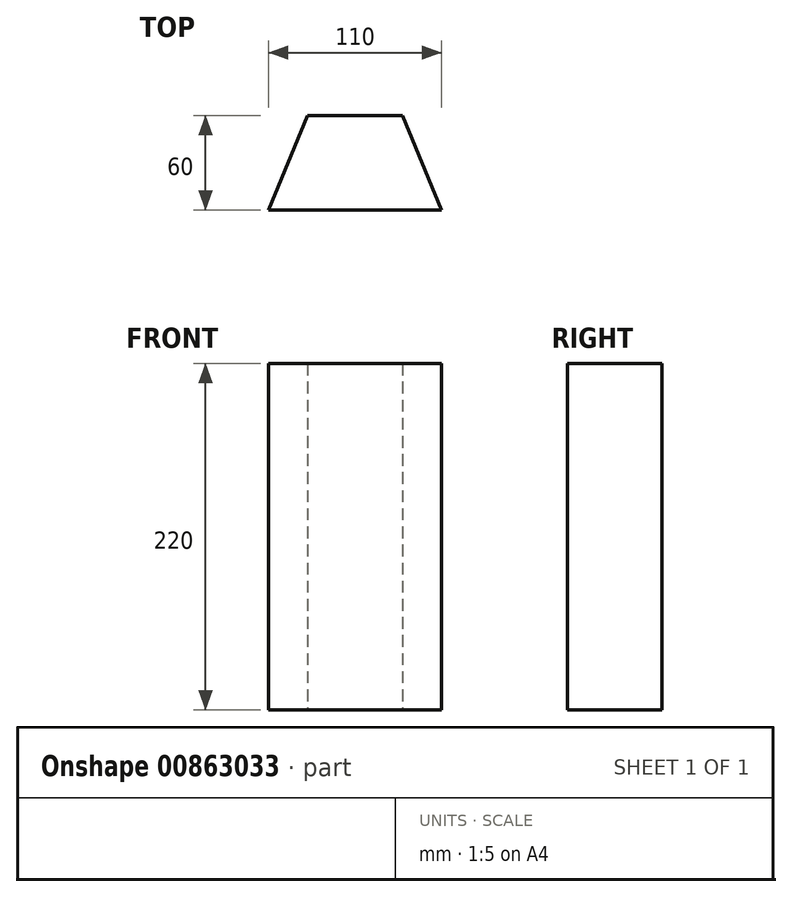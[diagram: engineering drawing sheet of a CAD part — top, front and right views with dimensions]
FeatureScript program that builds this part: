
annotation { "Feature Type Name" : "Feature", "Feature Type Description" : "" }
export const myFeature = defineFeature(function(context is Context, id is Id, definition is map)
    precondition{}
    {
        {
            var Q0;
            Q0=qCreatedBy(makeId("Top.planeOp"),FACE);
            var sketch = newSketch(context, id + "F0", { "sketchPlane" : qUnion([Q0])});
            skLineSegment(sketch, "E0.bottom", {"start": v(55, -60) * mm, "end": v(0, -60) * mm});
            skLineSegment(sketch, "E0.top", {"start": v(30.15, 0) * mm, "end": v(0, 0) * mm});
            skPoint(sketch, "E0.middle", {"position": v(0, 0) * mm});
            skLineSegment(sketch, "E1", {"start": v(55, -60) * mm, "end": v(30.15, 0) * mm});
            skLineSegment(sketch, "E2", {"start": v(0, -60) * mm, "end": v(0, 0) * mm, "construction": true});
            skLineSegment(sketch, "E3.MirrorCS", {"start": v(-55, -60) * mm, "end": v(0, -60) * mm});
            skLineSegment(sketch, "E4.MirrorCS", {"start": v(-55, -60) * mm, "end": v(-30.15, 0) * mm});
            skLineSegment(sketch, "E5.MirrorCS", {"start": v(-30.15, 0) * mm, "end": v(0, 0) * mm});
            skSolve(sketch);
        }
        {
            var Q0;
            Q0 = qSketchRegion(id + "F0", true);
            extrude(context, id + "F1", {"entities" : qUnion([Q0]), "depth" : 220 * mm, "offsetDistance" : 25 * mm});
        }
    });
